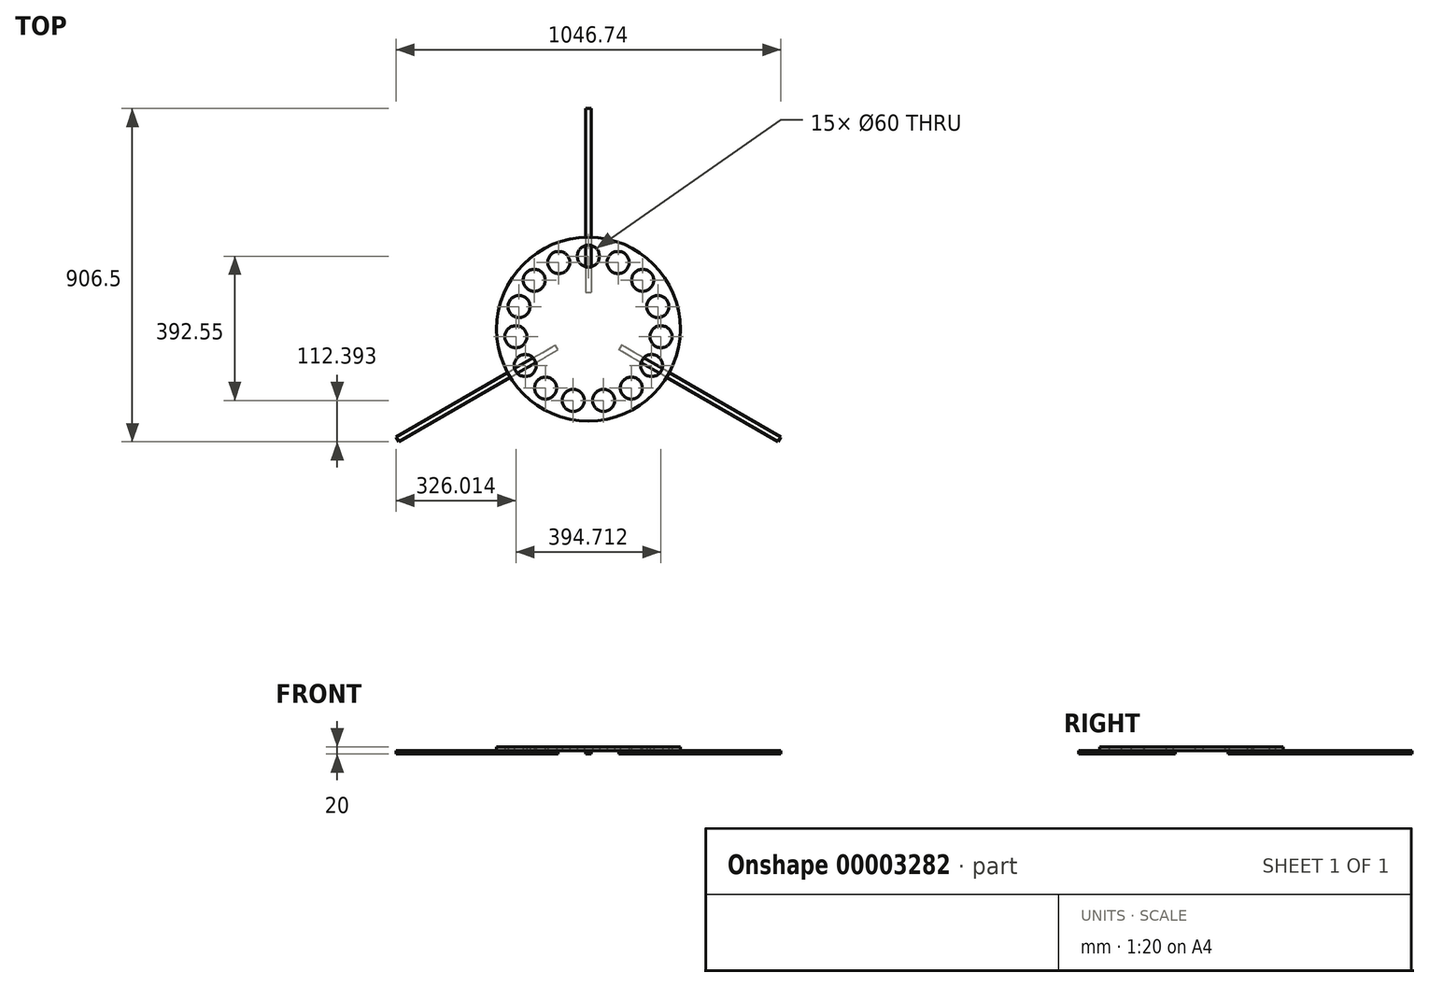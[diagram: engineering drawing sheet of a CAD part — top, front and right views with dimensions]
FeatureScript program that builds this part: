
annotation { "Feature Type Name" : "Feature", "Feature Type Description" : "" }
export const myFeature = defineFeature(function(context is Context, id is Id, definition is map)
    precondition{}
    {
        {
            var Q0;
            Q0=qCreatedBy(makeId("Top.planeOp"),FACE);
            var sketch = newSketch(context, id + "F0", { "sketchPlane" : qUnion([Q0])});
            skCircle(sketch, "E0", {"center": v(0, 0) * mm, "radius": 250 * mm});
            skCircle(sketch, "E1", {"center": v(0, 198.44) * mm, "radius": 30 * mm});
            skSolve(sketch);
        }
        {
            var Q0;
            Q0=makeQuery(id+"F0.imprint","IMPRINT",FACE,{"disambiguationData":[TD([[makeQuery(id+"F0.imprint","IMPRINT",EDGE,{"derivedFrom":sQuery(id+"F0.wireOp",EDGE,"E0")}),1.0]])]});
            extrude(context, id + "F1", {"entities" : qUnion([Q0]), "depth" : 10 * mm});
        }
        {
            var Q0;
            Q0=makeQuery(id+"F1.opExtrude","SWEPT_FACE",FACE,{"disambiguationData":[OSD([sQuery(id+"F0.wireOp",EDGE,"E1")])]});
            var Q1;
            Q1=makeQuery(id+"F1.opExtrude","SWEPT_BODY",BODY,{"disambiguationData":[OSD([sQuery(id+"F0.wireOp",EDGE,"E0"),sQuery(id+"F0.wireOp",EDGE,"E1")])]});
            var Q2;
            Q2=makeQuery(id+"F1.opExtrude","CAP_EDGE",EDGE,{"disambiguationData":[OSD([sQuery(id+"F0.wireOp",EDGE,"E0")])],"isStart":false});
            circularPattern(context, id + "F2", {"faces" : qUnion([Q0]), "axis" : qUnion([Q2]), "angle" : 360 * degree, "instanceCount" : 15, "equalSpace" : true, "patternType" : PatternType.FACE});
        }
        {
            var Q0;
            Q0=qCreatedBy(makeId("Top.planeOp"),FACE);
            var sketch = newSketch(context, id + "F3", { "sketchPlane" : qUnion([Q0])});
            skLineSegment(sketch, "E2.bottom", {"start": v(-515.87, -306.5) * mm, "end": v(-82.85, -56.5) * mm});
            skLineSegment(sketch, "E2.top", {"start": v(-523.37, -293.5) * mm, "end": v(-90.35, -43.5) * mm});
            skLineSegment(sketch, "E2.left", {"start": v(-515.87, -306.5) * mm, "end": v(-523.37, -293.5) * mm});
            skLineSegment(sketch, "E2.right", {"start": v(-82.85, -56.5) * mm, "end": v(-90.35, -43.5) * mm});
            skLineSegment(sketch, "E3", {"start": v(0, 0) * mm, "end": v(-313.67, -181.1) * mm, "construction": true});
            skLineSegment(sketch, "E4", {"start": v(0, 0) * mm, "end": v(-387.62, 0) * mm, "construction": true});
            skPoint(sketch, "E5", {"position": v(0, 0) * mm});
            skLineSegment(sketch, "E6.1.0", {"start": v(90.35, -43.5) * mm, "end": v(82.85, -56.5) * mm});
            skLineSegment(sketch, "E6.1.1", {"start": v(515.87, -306.5) * mm, "end": v(82.85, -56.5) * mm});
            skLineSegment(sketch, "E6.1.2", {"start": v(523.37, -293.5) * mm, "end": v(90.35, -43.5) * mm});
            skLineSegment(sketch, "E6.1.3", {"start": v(523.37, -293.5) * mm, "end": v(515.87, -306.5) * mm});
            skLineSegment(sketch, "E6.2.0", {"start": v(-7.5, 100) * mm, "end": v(7.5, 100) * mm});
            skLineSegment(sketch, "E6.2.1", {"start": v(7.5, 600) * mm, "end": v(7.5, 100) * mm});
            skLineSegment(sketch, "E6.2.2", {"start": v(-7.5, 600) * mm, "end": v(-7.5, 100) * mm});
            skLineSegment(sketch, "E6.2.3", {"start": v(-7.5, 600) * mm, "end": v(7.5, 600) * mm});
            skSolve(sketch);
        }
        {
            var Q0;
            {Q0=qUnion([makeQuery(id+"F3.imprint","IMPRINT",FACE,{"disambiguationData":[TD([[makeQuery(id+"F3.imprint","IMPRINT",EDGE,{"derivedFrom":sQuery(id+"F3.wireOp",EDGE,"E2.bottom")}),1.0]])]}),makeQuery(id+"F3.imprint","IMPRINT",FACE,{"disambiguationData":[TD([[makeQuery(id+"F3.imprint","IMPRINT",EDGE,{"derivedFrom":sQuery(id+"F3.wireOp",EDGE,"E6.1.0")}),1.0]])]}),makeQuery(id+"F3.imprint","IMPRINT",FACE,{"disambiguationData":[TD([[makeQuery(id+"F3.imprint","IMPRINT",EDGE,{"derivedFrom":sQuery(id+"F3.wireOp",EDGE,"E6.2.0")}),1.0]])]})]);}
            var Q1;
            Q1=makeQuery(id+"F1.opExtrude","CAP_FACE",FACE,{"disambiguationData":[OSD([sQuery(id+"F0.wireOp",EDGE,"E0"),sQuery(id+"F0.wireOp",EDGE,"E1")])],"isStart":false});
            extrude(context, id + "F4", {"entities" : qUnion([Q0]), "oppositeDirection" : true, "endBoundEntity" : qUnion([Q1]), "depth" : 10 * mm});
        }
    });
